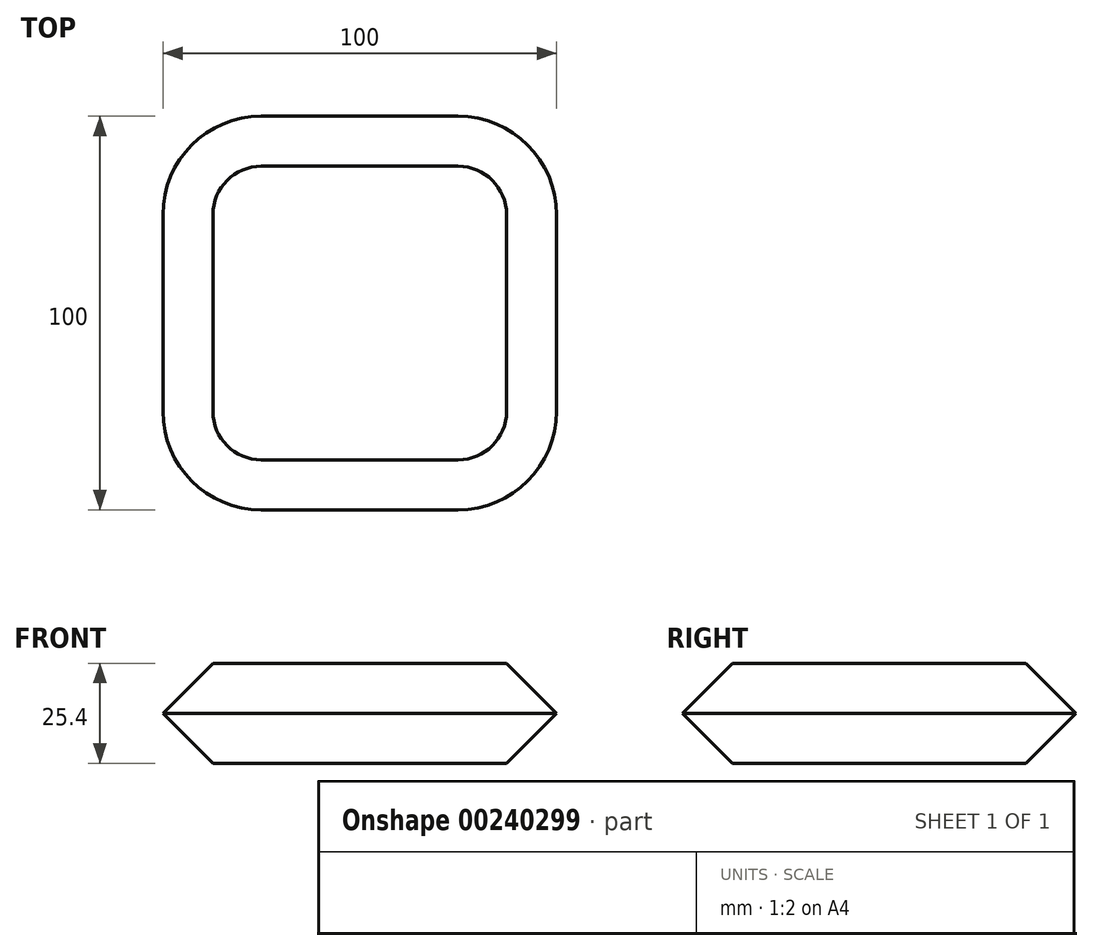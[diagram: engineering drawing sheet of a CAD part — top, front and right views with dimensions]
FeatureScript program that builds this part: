
annotation { "Feature Type Name" : "Feature", "Feature Type Description" : "" }
export const myFeature = defineFeature(function(context is Context, id is Id, definition is map)
    precondition{}
    {
        {
            var Q0;
            Q0=qCreatedBy(makeId("Top.planeOp"),FACE);
            var sketch = newSketch(context, id + "F0", { "sketchPlane" : qUnion([Q0])});
            skLineSegment(sketch, "E0.bottom", {"start": v(25, 50) * mm, "end": v(-25, 50) * mm});
            skLineSegment(sketch, "E0.top", {"start": v(25, -50) * mm, "end": v(-25, -50) * mm});
            skLineSegment(sketch, "E0.left", {"start": v(50, 25) * mm, "end": v(50, -25) * mm});
            skLineSegment(sketch, "E0.right", {"start": v(-50, 25) * mm, "end": v(-50, -25) * mm});
            skPoint(sketch, "E0.middle", {"position": v(0, 0) * mm});
            skPoint(sketch, "E1.visualSharp", {"position": v(-50, 50) * mm});
            skArc(sketch, "E1.filletArc", {"start": v(-25, 50) * mm, "mid": v(-42.68, 42.68) * mm, "end": v(-50, 25) * mm});
            skPoint(sketch, "E2.visualSharp", {"position": v(-50, -50) * mm});
            skArc(sketch, "E2.filletArc", {"start": v(-50, -25) * mm, "mid": v(-42.68, -42.68) * mm, "end": v(-25, -50) * mm});
            skPoint(sketch, "E3.visualSharp", {"position": v(50, -50) * mm});
            skArc(sketch, "E3.filletArc", {"start": v(25, -50) * mm, "mid": v(42.68, -42.68) * mm, "end": v(50, -25) * mm});
            skPoint(sketch, "E4.visualSharp", {"position": v(50, 50) * mm});
            skArc(sketch, "E4.filletArc", {"start": v(50, 25) * mm, "mid": v(42.68, 42.68) * mm, "end": v(25, 50) * mm});
            skSolve(sketch);
        }
        {
            var Q0;
            Q0 = qSketchRegion(id + "F0", true);
            extrude(context, id + "F1", {"entities" : qUnion([Q0]), "depth" : 25.4 * mm});
        }
        {
            var Q0;
            Q0=makeQuery(id+"F1.opExtrude","CAP_FACE",FACE,{"disambiguationData":[OSD([sQuery(id+"F0.wireOp",EDGE,"E0.bottom"),sQuery(id+"F0.wireOp",EDGE,"E0.top"),sQuery(id+"F0.wireOp",EDGE,"E0.left"),sQuery(id+"F0.wireOp",EDGE,"E0.right"),sQuery(id+"F0.wireOp",EDGE,"E1.filletArc"),sQuery(id+"F0.wireOp",EDGE,"E2.filletArc"),sQuery(id+"F0.wireOp",EDGE,"E3.filletArc"),sQuery(id+"F0.wireOp",EDGE,"E4.filletArc")])],"isStart":false});
            var Q1;
            Q1=makeQuery(id+"F1.opExtrude","CAP_FACE",FACE,{"disambiguationData":[OSD([sQuery(id+"F0.wireOp",EDGE,"E0.bottom"),sQuery(id+"F0.wireOp",EDGE,"E0.top"),sQuery(id+"F0.wireOp",EDGE,"E0.left"),sQuery(id+"F0.wireOp",EDGE,"E0.right"),sQuery(id+"F0.wireOp",EDGE,"E1.filletArc"),sQuery(id+"F0.wireOp",EDGE,"E2.filletArc"),sQuery(id+"F0.wireOp",EDGE,"E3.filletArc"),sQuery(id+"F0.wireOp",EDGE,"E4.filletArc")])],"isStart":true});
            chamfer(context, id + "F2", {"entities" : qUnion([Q0, Q1]), "width" : 12.7 * mm, "tangentPropagation" : true});
        }
    });
